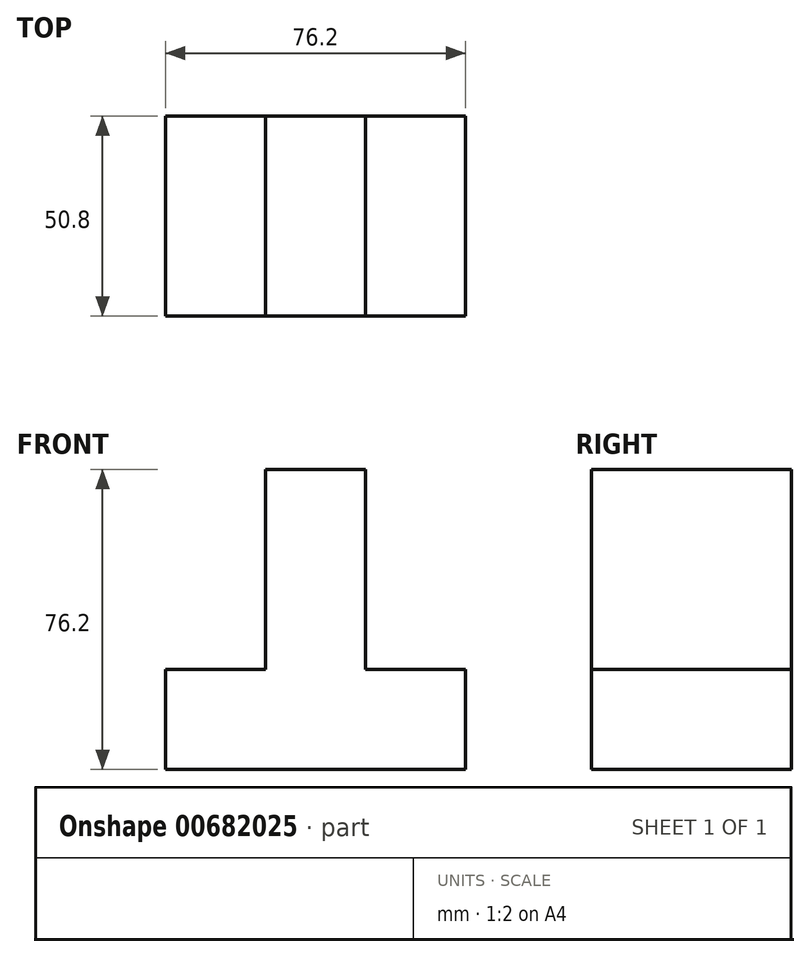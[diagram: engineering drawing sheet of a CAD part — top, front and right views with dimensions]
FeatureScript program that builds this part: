
annotation { "Feature Type Name" : "Feature", "Feature Type Description" : "" }
export const myFeature = defineFeature(function(context is Context, id is Id, definition is map)
    precondition{}
    {
        {
            var Q0;
            Q0=qCreatedBy(makeId("Front.planeOp"),FACE);
            var sketch = newSketch(context, id + "F0", { "sketchPlane" : qUnion([Q0])});
            skLineSegment(sketch, "E0", {"start": v(-50.8, 29.24) * mm, "end": v(-50.8, 3.84) * mm});
            skLineSegment(sketch, "E1", {"start": v(-50.8, 3.84) * mm, "end": v(25.4, 3.84) * mm});
            skLineSegment(sketch, "E2", {"start": v(25.4, 3.84) * mm, "end": v(25.4, 29.24) * mm});
            skLineSegment(sketch, "E3", {"start": v(25.4, 29.24) * mm, "end": v(0, 29.24) * mm});
            skLineSegment(sketch, "E4", {"start": v(0, 29.24) * mm, "end": v(0, 80.04) * mm});
            skLineSegment(sketch, "E5", {"start": v(0, 80.04) * mm, "end": v(-25.4, 80.04) * mm});
            skLineSegment(sketch, "E6", {"start": v(-25.4, 80.04) * mm, "end": v(-25.4, 29.24) * mm});
            skLineSegment(sketch, "E7", {"start": v(-25.4, 29.24) * mm, "end": v(-50.8, 29.24) * mm});
            skSolve(sketch);
        }
        {
            var Q0;
            Q0 = qSketchRegion(id + "F0", true);
            extrude(context, id + "F1", {"entities" : qUnion([Q0]), "depth" : 50.8 * mm, "offsetDistance" : 25.4 * mm});
        }
    });
